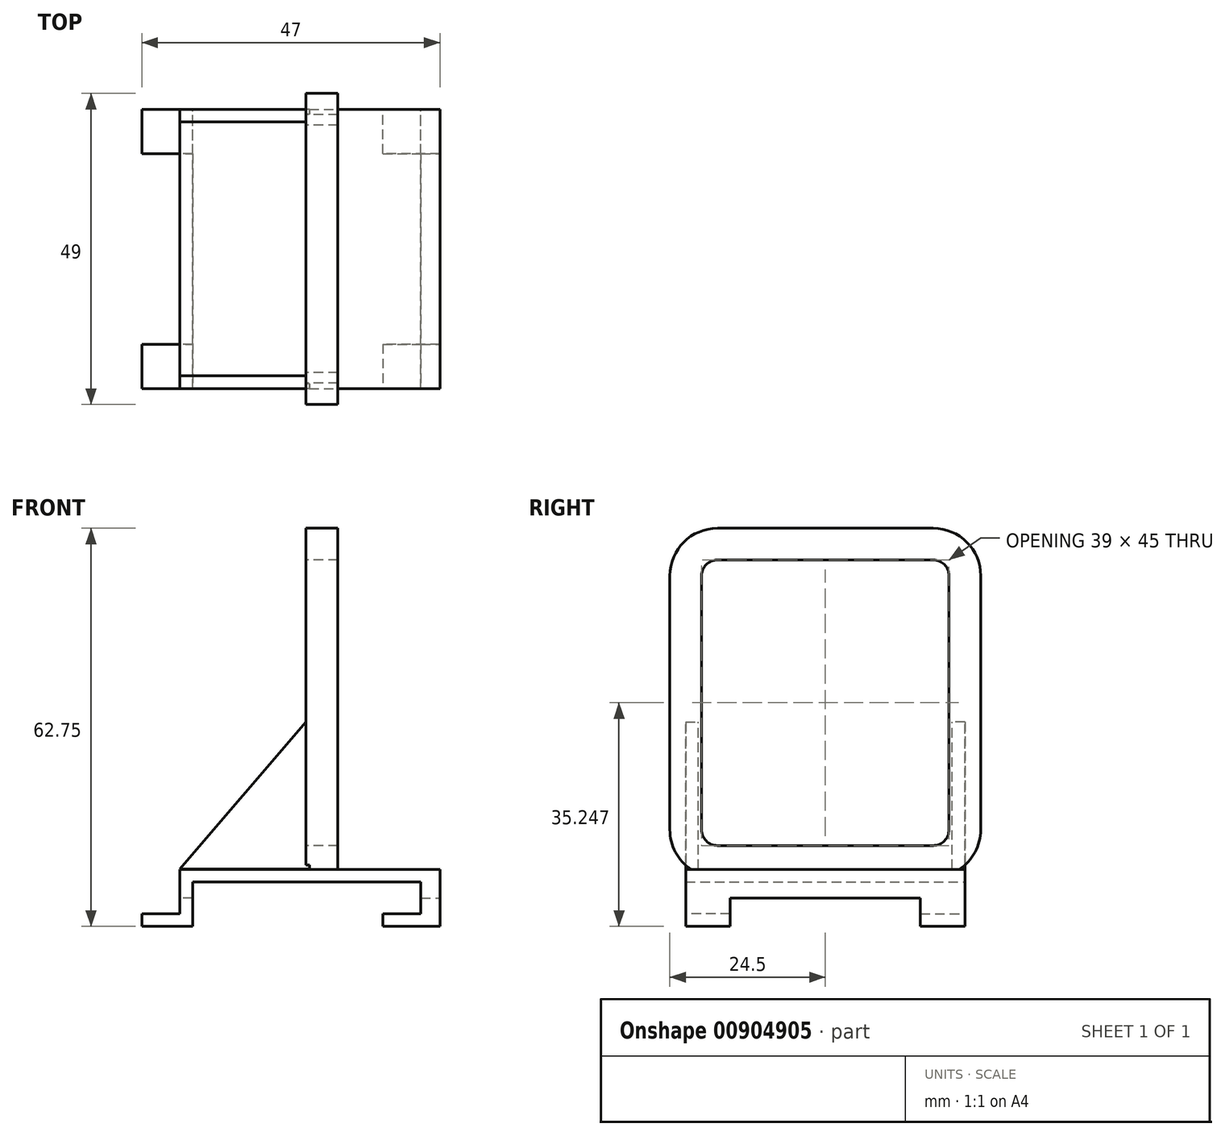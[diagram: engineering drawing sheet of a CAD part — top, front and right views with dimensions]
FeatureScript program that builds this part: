
annotation { "Feature Type Name" : "Feature", "Feature Type Description" : "" }
export const myFeature = defineFeature(function(context is Context, id is Id, definition is map)
    precondition{}
    {
        {
            var Q0;
            Q0=qCreatedBy(makeId("Front.planeOp"),FACE);
            var sketch = newSketch(context, id + "F0", { "sketchPlane" : qUnion([Q0])});
            skLineSegment(sketch, "E0", {"start": v(-28.4, 0) * mm, "end": v(-22.4, 0) * mm});
            skLineSegment(sketch, "E1", {"start": v(-22.4, 0) * mm, "end": v(-22.4, 7) * mm});
            skLineSegment(sketch, "E2", {"start": v(-22.4, 7) * mm, "end": v(18.6, 7) * mm});
            skLineSegment(sketch, "E3.0", {"start": v(-20.4, 5) * mm, "end": v(13.6, 5) * mm});
            skLineSegment(sketch, "E3.1", {"start": v(-20.4, -2) * mm, "end": v(-20.4, 5) * mm});
            skLineSegment(sketch, "E3.2", {"start": v(-28.4, -2) * mm, "end": v(-20.4, -2) * mm});
            skLineSegment(sketch, "E4", {"start": v(18.6, 7) * mm, "end": v(18.6, -2) * mm});
            skLineSegment(sketch, "E5", {"start": v(18.6, -2) * mm, "end": v(9.6, -2) * mm});
            skLineSegment(sketch, "E6", {"start": v(9.6, -2) * mm, "end": v(9.6, 0) * mm});
            skLineSegment(sketch, "E7", {"start": v(9.6, 0) * mm, "end": v(15.6, 0) * mm});
            skLineSegment(sketch, "E8", {"start": v(15.6, 0) * mm, "end": v(15.6, 5) * mm});
            skLineSegment(sketch, "E9", {"start": v(15.6, 5) * mm, "end": v(13.6, 5) * mm});
            skLineSegment(sketch, "E10", {"start": v(-28.4, -2) * mm, "end": v(-28.4, 0) * mm});
            skSolve(sketch);
        }
        {
            var Q0;
            Q0=makeQuery(id+"F0.imprint","IMPRINT",FACE,{"disambiguationData":[TD([[makeQuery(id+"F0.imprint","IMPRINT",EDGE,{"derivedFrom":sQuery(id+"F0.wireOp",EDGE,"E0")}),-1.0]])]});
            extrude(context, id + "F1", {"entities" : qUnion([Q0]), "depth" : 22 * mm, "offsetDistance" : 25 * mm});
        }
        {
            var Q0;
            Q0=makeQuery(id+"F1.opExtrude","CAP_FACE",FACE,{"disambiguationData":[OSD([sQuery(id+"F0.wireOp",EDGE,"E0"),sQuery(id+"F0.wireOp",EDGE,"E1"),sQuery(id+"F0.wireOp",EDGE,"E2"),sQuery(id+"F0.wireOp",EDGE,"E3.0"),sQuery(id+"F0.wireOp",EDGE,"E3.1"),sQuery(id+"F0.wireOp",EDGE,"E3.2"),sQuery(id+"F0.wireOp",EDGE,"E4"),sQuery(id+"F0.wireOp",EDGE,"E5"),sQuery(id+"F0.wireOp",EDGE,"E6"),sQuery(id+"F0.wireOp",EDGE,"E7"),sQuery(id+"F0.wireOp",EDGE,"E8"),sQuery(id+"F0.wireOp",EDGE,"E9"),sQuery(id+"F0.wireOp",EDGE,"E10")])],"isStart":false});
            var sketch = newSketch(context, id + "F2", { "sketchPlane" : qUnion([Q0])});
            skLineSegment(sketch, "E11", {"start": v(-22.4, 0) * mm, "end": v(-20.4, 0) * mm});
            skLineSegment(sketch, "E12", {"start": v(15.6, 0) * mm, "end": v(18.6, 0) * mm});
            skLineSegment(sketch, "E13", {"start": v(15.6, 2.5) * mm, "end": v(18.6, 2.5) * mm});
            skLineSegment(sketch, "E14", {"start": v(-20.4, 2.5) * mm, "end": v(-22.4, 2.5) * mm});
            skSolve(sketch);
        }
        {
            var Q0;
            Q0=qCreatedBy(makeId("Right.planeOp"),FACE);
            var sketch = newSketch(context, id + "F3", { "sketchPlane" : qUnion([Q0])});
            skLineSegment(sketch, "E15", {"start": v(-5, 8.25) * mm, "end": v(-22.25, 8.25) * mm});
            skLineSegment(sketch, "E16", {"start": v(0, 13.25) * mm, "end": v(0, 53.25) * mm});
            skLineSegment(sketch, "E17", {"start": v(-5, 58.25) * mm, "end": v(-22.25, 58.25) * mm});
            skPoint(sketch, "E18.visualSharp", {"position": v(0, 8.25) * mm});
            skArc(sketch, "E18.filletArc", {"start": v(-5, 8.25) * mm, "mid": v(-1.46, 9.71) * mm, "end": v(0, 13.25) * mm});
            skPoint(sketch, "E19.visualSharp", {"position": v(0, 58.25) * mm});
            skArc(sketch, "E19.filletArc", {"start": v(0, 53.25) * mm, "mid": v(-1.46, 56.78) * mm, "end": v(-5, 58.25) * mm});
            skSolve(sketch);
        }
        {
            var Q0;
            Q0=qSketchRegion(id+"F2",true);
            var Q1;
            {var subQ0=sQuery(id+"F2.wireOp",EDGE,"E11");Q1=makeQuery(id+"F2.imprint","IMPRINT",FACE,{"disambiguationData":[TD([[makeQuery(id+"F2.imprint","IMPRINT",EDGE,{"derivedFrom":subQ0}),-1.0]])]});}
            var Q2;
            {var subQ1=sQuery(id+"F2.wireOp",EDGE,"E12");Q2=makeQuery(id+"F2.imprint","IMPRINT",FACE,{"disambiguationData":[TD([[makeQuery(id+"F2.imprint","IMPRINT",EDGE,{"derivedFrom":subQ1}),-1.0]])]});}
            var Q3;
            {var subQ0=sQuery(id+"F2.wireOp",EDGE,"E11");Q3=makeQuery(id+"F2.imprint","IMPRINT",FACE,{"disambiguationData":[TD([[makeQuery(id+"F2.imprint","IMPRINT",EDGE,{"derivedFrom":subQ0}),1.0]])]});}
            var Q4;
            {var subQ0=sQuery(id+"F2.wireOp",EDGE,"E12");Q4=makeQuery(id+"F2.imprint","IMPRINT",FACE,{"disambiguationData":[TD([[makeQuery(id+"F2.imprint","IMPRINT",EDGE,{"derivedFrom":subQ0}),1.0]])]});}
            extrude(context, id + "F4", {"entities" : qUnion([Q0, Q1, Q2, Q3, Q4]), "operationType" : NewBodyOperationType.REMOVE, "oppositeDirection" : true, "depth" : 15 * mm, "offsetDistance" : 25 * mm});
        }
        {
            var Q0;
            {var subQ3=sQuery(id+"F2.wireOp",EDGE,"E13");Q0=makeQuery(id+"F2.imprint","IMPRINT",FACE,{"disambiguationData":[TD([[makeQuery(id+"F2.imprint","IMPRINT",EDGE,{"derivedFrom":subQ3}),1.0]])]});}
            cPlane(context, id + "F5", {"entities" : qUnion([Q0]), "cplaneType" : CPlaneType.OFFSET, "offset" : 0 * mm, "width" : 150 * mm, "height" : 150 * mm});
        }
        {
            var Q0;
            Q0=qCreatedBy(id+"F5.planeOp",FACE);
            var sketch = newSketch(context, id + "F6", { "sketchPlane" : qUnion([Q0])});
            skLineSegment(sketch, "E20.bottom", {"start": v(2.5, 5.75) * mm, "end": v(-2.5, 5.75) * mm});
            skLineSegment(sketch, "E20.top", {"start": v(2.5, 10.75) * mm, "end": v(-2.5, 10.75) * mm});
            skLineSegment(sketch, "E20.left", {"start": v(2.5, 5.75) * mm, "end": v(2.5, 10.75) * mm});
            skLineSegment(sketch, "E20.right", {"start": v(-2.5, 5.75) * mm, "end": v(-2.5, 10.75) * mm});
            skPoint(sketch, "E20.middle", {"position": v(0, 8.25) * mm});
            skSolve(sketch);
        }
        {
            var Q0;
            Q0=makeQuery(id+"F6.imprint","IMPRINT",FACE,{"disambiguationData":[TD([[makeQuery(id+"F6.imprint","IMPRINT",EDGE,{"derivedFrom":sQuery(id+"F6.wireOp",EDGE,"E20.bottom")}),-1.0]])]});
            var Q1;
            Q1=sQuery(id+"F3.wireOp",EDGE,"E15");
            var Q2;
            Q2=sQuery(id+"F3.wireOp",EDGE,"E18.filletArc");
            var Q3;
            Q3=sQuery(id+"F3.wireOp",EDGE,"E19.filletArc");
            var Q4;
            Q4=sQuery(id+"F3.wireOp",EDGE,"E17");
            var Q5;
            Q5=sQuery(id+"F3.wireOp",EDGE,"E16");
            sweep(context, id + "F7", {"operationType" : NewBodyOperationType.ADD, "profiles" : qUnion([Q0]), "path" : qUnion([Q1, Q2, Q3, Q4, Q5])});
        }
        {
            var Q0;
            Q0=qCreatedBy(makeId("Front.planeOp"),FACE);
            var sketch = newSketch(context, id + "F8", { "sketchPlane" : qUnion([Q0])});
            skLineSegment(sketch, "E21", {"start": v(-22.4, 7.05) * mm, "end": v(-1.95, 7.05) * mm});
            skLineSegment(sketch, "E22", {"start": v(-1.95, 7.05) * mm, "end": v(-1.95, 30.84) * mm});
            skLineSegment(sketch, "E23", {"start": v(-1.95, 30.84) * mm, "end": v(-22.4, 7.05) * mm});
            skSolve(sketch);
        }
        {
            var Q0;
            Q0 = qSketchRegion(id + "F8", true);
            extrude(context, id + "F9", {"entities" : qUnion([Q0]), "operationType" : NewBodyOperationType.ADD, "depth" : 2 * mm, "offsetDistance" : 25 * mm});
        }
        {
            var Q0;
            Q0=makeQuery(id+"F1.opExtrude","SWEPT_BODY",BODY,{"disambiguationData":[OSD([sQuery(id+"F0.wireOp",EDGE,"E0"),sQuery(id+"F0.wireOp",EDGE,"E1"),sQuery(id+"F0.wireOp",EDGE,"E2"),sQuery(id+"F0.wireOp",EDGE,"E3.0"),sQuery(id+"F0.wireOp",EDGE,"E3.1"),sQuery(id+"F0.wireOp",EDGE,"E3.2"),sQuery(id+"F0.wireOp",EDGE,"E4"),sQuery(id+"F0.wireOp",EDGE,"E5"),sQuery(id+"F0.wireOp",EDGE,"E6"),sQuery(id+"F0.wireOp",EDGE,"E7"),sQuery(id+"F0.wireOp",EDGE,"E8"),sQuery(id+"F0.wireOp",EDGE,"E9"),sQuery(id+"F0.wireOp",EDGE,"E10")])]});
            var Q1;
            Q1=qCreatedBy(id+"F5.planeOp",FACE);
            mirror(context, id + "F10", {"operationType" : NewBodyOperationType.ADD, "entities" : qUnion([Q0]), "mirrorPlane" : qUnion([Q1])});
        }
    });
